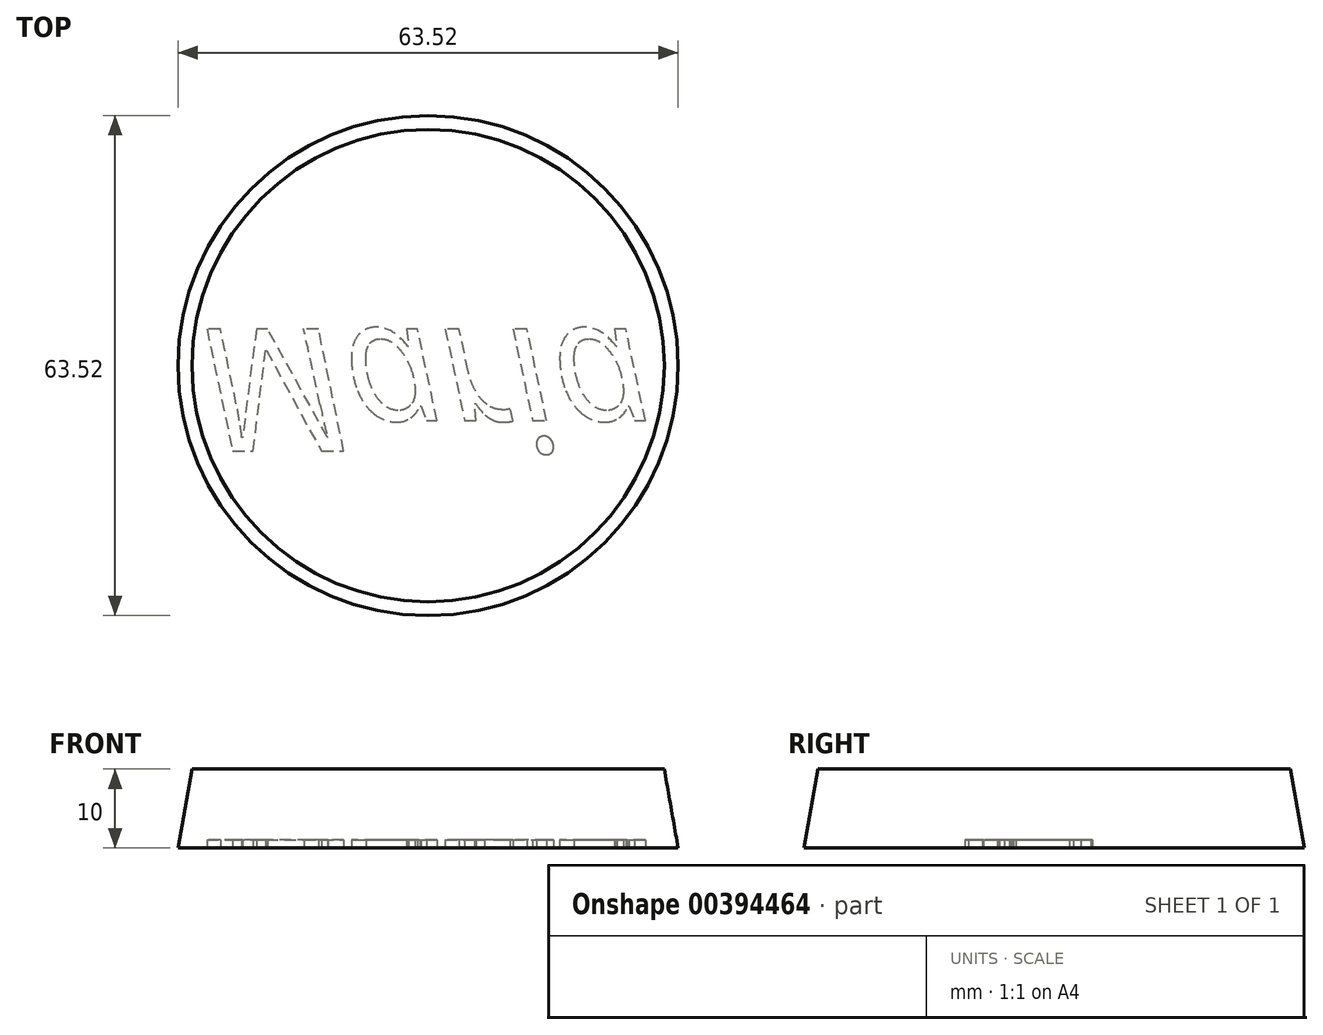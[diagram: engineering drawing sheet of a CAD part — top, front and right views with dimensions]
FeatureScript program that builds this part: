
annotation { "Feature Type Name" : "Feature", "Feature Type Description" : "" }
export const myFeature = defineFeature(function(context is Context, id is Id, definition is map)
    precondition{}
    {
        {
            var Q0;
            Q0=qCreatedBy(makeId("Top.planeOp"),FACE);
            var sketch = newSketch(context, id + "F0", { "sketchPlane" : qUnion([Q0])});
            skCircle(sketch, "E0", {"center": v(0, 0) * mm, "radius": 30 * mm});
            skSolve(sketch);
        }
        {
            var Q0;
            Q0=makeQuery(id+"F0.imprint","IMPRINT",FACE,{"disambiguationData":[TD([[makeQuery(id+"F0.imprint","IMPRINT",EDGE,{"derivedFrom":sQuery(id+"F0.wireOp",EDGE,"E0")}),1.0]])]});
            extrude(context, id + "F1", {"entities" : qUnion([Q0]), "oppositeDirection" : true, "depth" : 10 * mm, "hasDraft" : true, "draftAngle" : 10 * degree});
        }
        {
            var Q0;
            Q0=makeQuery(id+"F1.opExtrude","CAP_FACE",FACE,{"disambiguationData":[OSD([sQuery(id+"F0.wireOp",EDGE,"E0")])],"isStart":false});
            var sketch = newSketch(context, id + "F2", { "sketchPlane" : qUnion([Q0])});
            skText(sketch, "E1", { "text": "Maria", "fontName": "OpenSans-Italic.ttf"});
            const initialGuessF2  = {"E1": [-0.029, -0.00468, 1, 0, 0.01568]};
            skSetInitialGuess(sketch, initialGuessF2);
            skSolve(sketch);
        }
        {
            var Q0;
            Q0=qSketchRegion(id+"F2",true);
            extrude(context, id + "F3", {"entities" : qUnion([Q0]), "operationType" : NewBodyOperationType.REMOVE, "oppositeDirection" : true, "depth" : 1 * mm});
        }
    });
